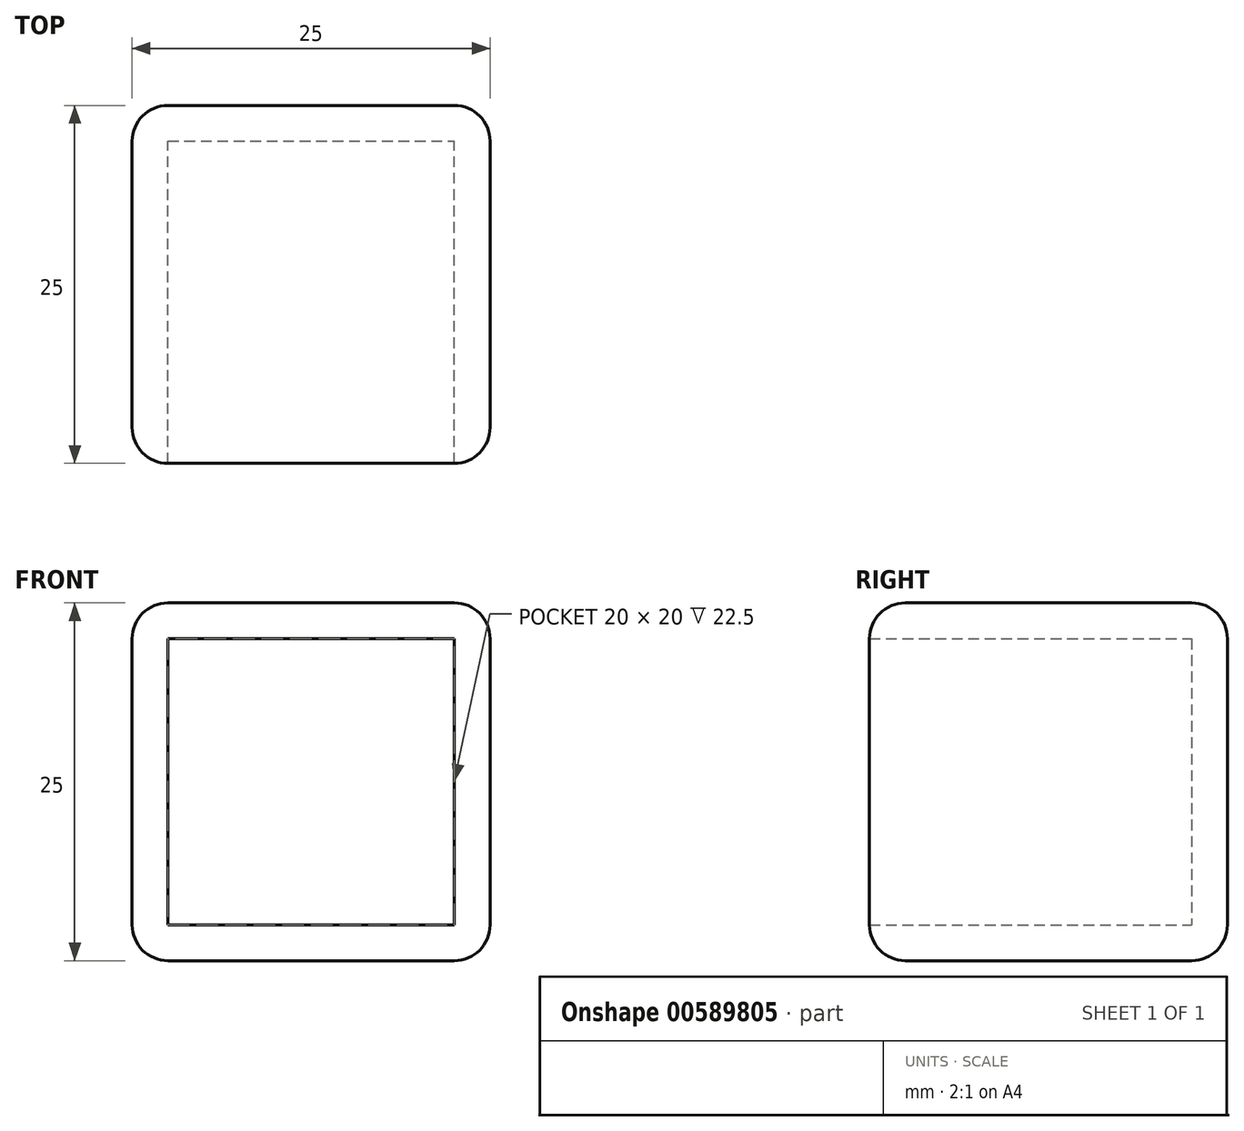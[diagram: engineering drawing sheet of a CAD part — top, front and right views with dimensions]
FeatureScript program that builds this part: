
annotation { "Feature Type Name" : "Feature", "Feature Type Description" : "" }
export const myFeature = defineFeature(function(context is Context, id is Id, definition is map)
    precondition{}
    {
        {
            var Q0;
            Q0=qCreatedBy(makeId("Top.planeOp"),FACE);
            var sketch = newSketch(context, id + "F0", { "sketchPlane" : qUnion([Q0])});
            skLineSegment(sketch, "E0.bottom", {"start": v(0, 0) * mm, "end": v(25, 0) * mm});
            skLineSegment(sketch, "E0.top", {"start": v(0, 25) * mm, "end": v(25, 25) * mm});
            skLineSegment(sketch, "E0.left", {"start": v(0, 0) * mm, "end": v(0, 25) * mm});
            skLineSegment(sketch, "E0.right", {"start": v(25, 0) * mm, "end": v(25, 25) * mm});
            skSolve(sketch);
        }
        {
            var Q0;
            Q0=makeQuery(id+"F0.imprint","IMPRINT",FACE,{"disambiguationData":[TD([[makeQuery(id+"F0.imprint","IMPRINT",EDGE,{"derivedFrom":sQuery(id+"F0.wireOp",EDGE,"E0.bottom")}),1.0]])]});
            extrude(context, id + "F1", {"entities" : qUnion([Q0]), "depth" : 25 * mm, "offsetDistance" : 25 * mm});
        }
        {
            var Q0;
            Q0=makeQuery(id+"F1.opExtrude","SWEPT_FACE",FACE,{"disambiguationData":[OSD([sQuery(id+"F0.wireOp",EDGE,"E0.bottom")])]});
            shell(context, id + "F2", {"entities" : qUnion([Q0]), "thickness" : 2.5 * mm});
        }
        {
            var Q0;
            Q0=makeQuery(id+"F1.opExtrude","CAP_EDGE",EDGE,{"disambiguationData":[OSD([sQuery(id+"F0.wireOp",EDGE,"E0.bottom")])],"isStart":false});
            var Q1;
            Q1=makeQuery(id+"F1.opExtrude","CAP_EDGE",EDGE,{"disambiguationData":[OSD([sQuery(id+"F0.wireOp",EDGE,"E0.right")])],"isStart":true});
            var Q2;
            Q2=makeQuery(id+"F1.opExtrude","CAP_EDGE",EDGE,{"disambiguationData":[OSD([sQuery(id+"F0.wireOp",EDGE,"E0.top")])],"isStart":true});
            var Q3;
            Q3=makeQuery(id+"F1.opExtrude","CAP_EDGE",EDGE,{"disambiguationData":[OSD([sQuery(id+"F0.wireOp",EDGE,"E0.left")])],"isStart":true});
            var Q4;
            Q4=makeQuery(id+"F1.opExtrude","CAP_EDGE",EDGE,{"disambiguationData":[OSD([sQuery(id+"F0.wireOp",EDGE,"E0.right")])],"isStart":false});
            var Q5;
            Q5=makeQuery(id+"F1.opExtrude","CAP_EDGE",EDGE,{"disambiguationData":[OSD([sQuery(id+"F0.wireOp",EDGE,"E0.top")])],"isStart":false});
            var Q6;
            Q6=makeQuery(id+"F1.opExtrude","SWEPT_FACE",FACE,{"disambiguationData":[OSD([sQuery(id+"F0.wireOp",EDGE,"E0.left")])]});
            var Q7;
            Q7=makeQuery(id+"F1.opExtrude","SWEPT_FACE",FACE,{"disambiguationData":[OSD([sQuery(id+"F0.wireOp",EDGE,"E0.right")])]});
            var Q8;
            Q8=makeQuery(id+"F1.opExtrude","CAP_FACE",FACE,{"disambiguationData":[OSD([sQuery(id+"F0.wireOp",EDGE,"E0.bottom"),sQuery(id+"F0.wireOp",EDGE,"E0.top"),sQuery(id+"F0.wireOp",EDGE,"E0.left"),sQuery(id+"F0.wireOp",EDGE,"E0.right")])],"isStart":false});
            var Q9;
            Q9=makeQuery(id+"F1.opExtrude","SWEPT_FACE",FACE,{"disambiguationData":[OSD([sQuery(id+"F0.wireOp",EDGE,"E0.top")])]});
            var Q10;
            Q10=makeQuery(id+"F1.opExtrude","CAP_EDGE",EDGE,{"disambiguationData":[OSD([sQuery(id+"F0.wireOp",EDGE,"E0.bottom")])],"isStart":true});
            var Q11;
            Q11=makeQuery(id+"F1.opExtrude","CAP_FACE",FACE,{"disambiguationData":[OSD([sQuery(id+"F0.wireOp",EDGE,"E0.bottom"),sQuery(id+"F0.wireOp",EDGE,"E0.top"),sQuery(id+"F0.wireOp",EDGE,"E0.left"),sQuery(id+"F0.wireOp",EDGE,"E0.right")])],"isStart":true});
            fillet(context, id + "F3", {"entities" : qUnion([Q0, Q1, Q2, Q3, Q4, Q5, Q6, Q7, Q8, Q9, Q10, Q11]), "radius" : 2.5 * mm, "tangentPropagation" : true, "allowEdgeOverflow" : false});
        }
    });
